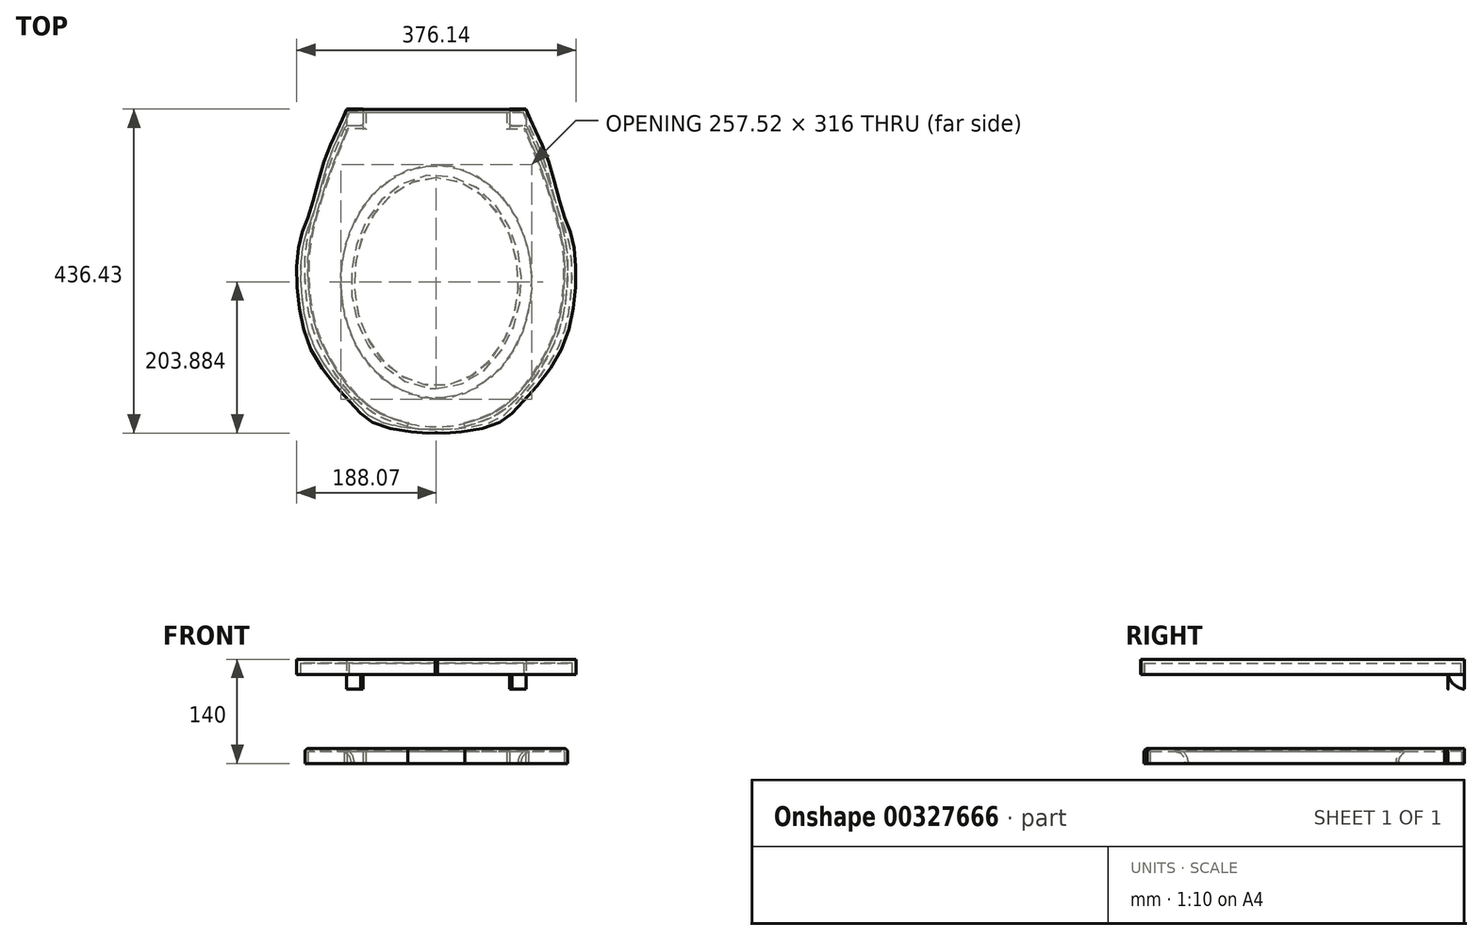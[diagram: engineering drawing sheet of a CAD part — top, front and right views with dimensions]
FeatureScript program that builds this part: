
annotation { "Feature Type Name" : "Feature", "Feature Type Description" : "" }
export const myFeature = defineFeature(function(context is Context, id is Id, definition is map)
    precondition{}
    {
        {
            var Q0;
            Q0=qCreatedBy(makeId("Top.planeOp"),FACE);
            var sketch = newSketch(context, id + "F0", { "sketchPlane" : qUnion([Q0])});
            skEllipse(sketch, "E0", {"center": v(236.1, 282.98) * mm, "majorRadius": 140 * mm, "minorRadius": 110.76 * mm, "majorAxis": v(0, 1)});
            skLineSegment(sketch, "E1", {"start": v(115.12, 515.5) * mm, "end": v(236.1, 515.5) * mm});
            skFitSpline(sketch, "E2", {"points": [v(115.12, 515.5) * mm, v(87.79, 448.56) * mm, v(66.11, 379.92) * mm, v(54.24, 335.02) * mm, v(53.21, 266.89) * mm, v(77.73, 184.39) * mm, v(125, 119.02) * mm, v(164.89, 92.63) * mm, v(226.57, 79.74) * mm, v(235.17, 79.43) * mm, v(240.38, 79.43) * mm], "startDerivative": vector(-235.73, -539.67) * mm, "endDerivative": vector(163.45, -0.98) * mm});
            skLineSegment(sketch, "E3", {"start": v(236.1, 515.5) * mm, "end": v(236.1, 282.98) * mm, "construction": true});
            skFitSpline(sketch, "E4.MirrorCS", {"points": [v(357.1, 515.5) * mm, v(384.43, 448.56) * mm, v(406.1, 379.92) * mm, v(417.98, 335.02) * mm, v(419, 266.89) * mm, v(394.49, 184.39) * mm, v(347.22, 119.02) * mm, v(307.33, 92.63) * mm, v(245.65, 79.74) * mm, v(237.05, 79.43) * mm, v(231.84, 79.43) * mm], "startDerivative": vector(235.73, -539.67) * mm, "endDerivative": vector(-163.45, -0.98) * mm});
            skLineSegment(sketch, "E5.MirrorCS", {"start": v(357.1, 515.5) * mm, "end": v(236.1, 515.5) * mm});
            skLineSegment(sketch, "E6", {"start": v(137.44, 515.5) * mm, "end": v(137.44, 493.2) * mm});
            skLineSegment(sketch, "E7", {"start": v(137.44, 493.2) * mm, "end": v(117.65, 493.2) * mm});
            skLineSegment(sketch, "E8", {"start": v(236.1, 282.98) * mm, "end": v(236.1, 61.07) * mm, "construction": true});
            skArc(sketch, "E9", {"start": v(117.65, 493.2) * mm, "mid": v(114.06, 491.98) * mm, "end": v(111.95, 488.82) * mm});
            skLineSegment(sketch, "E10", {"start": v(236.1, 83.72) * mm, "end": v(197.51, 88.12) * mm, "construction": true});
            skArc(sketch, "E11", {"start": v(197.51, 88.12) * mm, "mid": v(216.69, 84.82) * mm, "end": v(236.1, 83.72) * mm});
            skFitSpline(sketch, "E12", {"points": [v(197.51, 88.12) * mm, v(160.98, 100.68) * mm, v(121.9, 130.72) * mm, v(84.87, 184.45) * mm, v(64.85, 239.02) * mm, v(59.04, 301.02) * mm, v(63.56, 345.58) * mm, v(87.45, 426.95) * mm, v(111.95, 488.82) * mm], "startDerivative": vector(-360.52, 97.38) * mm, "endDerivative": vector(181.28, 430.4) * mm});
            skLineSegment(sketch, "E13.MirrorCS", {"start": v(334.78, 493.2) * mm, "end": v(354.57, 493.2) * mm});
            skLineSegment(sketch, "E14.MirrorCS", {"start": v(334.78, 515.5) * mm, "end": v(334.78, 493.2) * mm});
            skArc(sketch, "E15.MirrorCS", {"start": v(354.57, 493.2) * mm, "mid": v(358.16, 491.98) * mm, "end": v(360.27, 488.82) * mm});
            skFitSpline(sketch, "E16.MirrorCS", {"points": [v(274.7, 88.12) * mm, v(311.24, 100.68) * mm, v(350.31, 130.72) * mm, v(387.35, 184.45) * mm, v(407.37, 239.02) * mm, v(413.18, 301.02) * mm, v(408.66, 345.58) * mm, v(384.77, 426.95) * mm, v(360.27, 488.82) * mm], "startDerivative": vector(360.52, 97.38) * mm, "endDerivative": vector(-181.28, 430.4) * mm});
            skArc(sketch, "E17.MirrorCS", {"start": v(274.7, 88.12) * mm, "mid": v(255.53, 84.82) * mm, "end": v(236.1, 83.72) * mm});
            skLineSegment(sketch, "E18.MirrorCS", {"start": v(236.1, 83.72) * mm, "end": v(274.7, 88.12) * mm, "construction": true});
            skSolve(sketch);
        }
        {
            var Q0;
            Q0=makeQuery(id+"F0.imprint","IMPRINT",FACE,{"disambiguationData":[TD([[makeQuery(id+"F0.imprint","IMPRINT",EDGE,{"derivedFrom":sQuery(id+"F0.wireOp",EDGE,"E0")}),-1.0]])]});
            extrude(context, id + "F1", {"entities" : qUnion([Q0]), "depth" : 20 * mm});
        }
        {
            var Q0;
            Q0=makeQuery(id+"F1.opExtrude","CAP_EDGE",EDGE,{"disambiguationData":[OSD([sQuery(id+"F0.wireOp",EDGE,"E0")])],"isStart":false});
            fillet(context, id + "F2", {"entities" : qUnion([Q0]), "radius" : 18 * mm, "tangentPropagation" : true, "allowEdgeOverflow" : false});
        }
        {
            var Q0;
            Q0=makeQuery(id+"F1.opExtrude","CAP_EDGE",EDGE,{"disambiguationData":[OSD([sQuery(id+"F0.wireOp",EDGE,"E12")])],"isStart":false});
            var Q1;
            Q1=makeQuery(id+"F1.opExtrude","CAP_EDGE",EDGE,{"disambiguationData":[OSD([sQuery(id+"F0.wireOp",EDGE,"E11"),sQuery(id+"F0.wireOp",EDGE,"E17.MirrorCS")])],"isStart":false});
            var Q2;
            Q2=makeQuery(id+"F1.opExtrude","CAP_EDGE",EDGE,{"disambiguationData":[OSD([sQuery(id+"F0.wireOp",EDGE,"E16.MirrorCS")])],"isStart":false});
            var Q3;
            Q3=makeQuery(id+"F1.opExtrude","CAP_EDGE",EDGE,{"disambiguationData":[OSD([sQuery(id+"F0.wireOp",EDGE,"E15.MirrorCS")])],"isStart":false});
            var Q4;
            Q4=makeQuery(id+"F1.opExtrude","CAP_EDGE",EDGE,{"disambiguationData":[OSD([sQuery(id+"F0.wireOp",EDGE,"E13.MirrorCS")])],"isStart":false});
            var Q5;
            Q5=makeQuery(id+"F1.opExtrude","CAP_EDGE",EDGE,{"disambiguationData":[OSD([sQuery(id+"F0.wireOp",EDGE,"E9")])],"isStart":false});
            var Q6;
            Q6=makeQuery(id+"F1.opExtrude","CAP_EDGE",EDGE,{"disambiguationData":[OSD([sQuery(id+"F0.wireOp",EDGE,"E7")])],"isStart":false});
            fillet(context, id + "F3", {"entities" : qUnion([Q0, Q1, Q2, Q3, Q4, Q5, Q6]), "radius" : 5 * mm, "tangentPropagation" : true, "allowEdgeOverflow" : false});
        }
        {
            var Q0;
            Q0=makeQuery(id+"F1.opExtrude","CAP_FACE",FACE,{"disambiguationData":[OSD([sQuery(id+"F0.wireOp",EDGE,"E0"),sQuery(id+"F0.wireOp",EDGE,"E1"),sQuery(id+"F0.wireOp",EDGE,"E5.MirrorCS"),sQuery(id+"F0.wireOp",EDGE,"E6"),sQuery(id+"F0.wireOp",EDGE,"E7"),sQuery(id+"F0.wireOp",EDGE,"98a317c4-5fe9-485b-bc22-271dbf30fffc"),sQuery(id+"F0.wireOp",EDGE,"01ff45cd-890d-4195-a086-3f56b90537150.MirrorCS"),sQuery(id+"F0.wireOp",EDGE,"01ff45cd-890d-4195-a086-3f56b90537151.MirrorCS"),sQuery(id+"F0.wireOp",EDGE,"01ff45cd-890d-4195-a086-3f56b90537152.MirrorCS")])],"isStart":true});
            shell(context, id + "F4", {"entities" : qUnion([Q0]), "thickness" : 4 * mm});
        }
        {
            var Q0;
            Q0=makeQuery(id+"F1.opExtrude","CAP_FACE",FACE,{"disambiguationData":[OSD([sQuery(id+"F0.wireOp",EDGE,"E0"),sQuery(id+"F0.wireOp",EDGE,"E1"),sQuery(id+"F0.wireOp",EDGE,"E5.MirrorCS"),sQuery(id+"F0.wireOp",EDGE,"E6"),sQuery(id+"F0.wireOp",EDGE,"E7"),sQuery(id+"F0.wireOp",EDGE,"E9"),sQuery(id+"F0.wireOp",EDGE,"E11"),sQuery(id+"F0.wireOp",EDGE,"E12"),sQuery(id+"F0.wireOp",EDGE,"E13.MirrorCS"),sQuery(id+"F0.wireOp",EDGE,"E14.MirrorCS"),sQuery(id+"F0.wireOp",EDGE,"E15.MirrorCS"),sQuery(id+"F0.wireOp",EDGE,"E16.MirrorCS"),sQuery(id+"F0.wireOp",EDGE,"E17.MirrorCS")])],"isStart":false});
            cPlane(context, id + "F5", {"entities" : qUnion([Q0]), "cplaneType" : CPlaneType.OFFSET, "offset" : 100 * mm, "width" : 150 * mm, "height" : 150 * mm});
        }
        {
            var Q0;
            Q0=qCreatedBy(id+"F5.planeOp",FACE);
            var sketch = newSketch(context, id + "F6", { "sketchPlane" : qUnion([Q0])});
            skLineSegment(sketch, "E19.0.0", {"start": v(357.1, 515.5) * mm, "end": v(334.78, 515.5) * mm});
            skLineSegment(sketch, "E19.0.11", {"start": v(137.44, 515.5) * mm, "end": v(115.12, 515.5) * mm});
            skFitSpline(sketch, "E19.0.12", {"points": [v(115.12, 515.5) * mm, v(105.63, 493.78) * mm, v(86.66, 450.36) * mm, v(66.5, 379.75) * mm, v(51.66, 335.52) * mm, v(49.53, 264.45) * mm, v(71.71, 183.3) * mm, v(123.62, 116.85) * mm, v(159.22, 89.72) * mm, v(225.54, 79.1) * mm, v(234.58, 79.47) * mm, v(238.62, 79.44) * mm, v(240.38, 79.43) * mm]});
            skFitSpline(sketch, "E19.0.13", {"points": [v(231.84, 79.43) * mm, v(233.6, 79.44) * mm, v(237.64, 79.47) * mm, v(246.68, 79.1) * mm, v(313, 89.72) * mm, v(348.6, 116.85) * mm, v(400.5, 183.3) * mm, v(422.7, 264.45) * mm, v(420.56, 335.52) * mm, v(405.71, 379.75) * mm, v(385.56, 450.36) * mm, v(366.6, 493.78) * mm, v(357.1, 515.5) * mm]});
            skLineSegment(sketch, "E20.0", {"start": v(334.78, 515.5) * mm, "end": v(137.44, 515.5) * mm});
            skLineSegment(sketch, "E21.0", {"start": v(357.1, 515.5) * mm, "end": v(236.1, 515.5) * mm});
            skLineSegment(sketch, "E22.0", {"start": v(115.12, 515.5) * mm, "end": v(236.1, 515.5) * mm});
            skPoint(sketch, "E19.0.10.start.orphan", {"position": v(137.44, 493.2) * mm});
            skPoint(sketch, "E23.orphan", {"position": v(137.44, 488.2) * mm});
            skPoint(sketch, "E19.0.8.end.orphan", {"position": v(117.65, 493.2) * mm});
            skPoint(sketch, "E19.0.7.end.orphan", {"position": v(111.95, 488.82) * mm});
            skPoint(sketch, "E19.0.1.end.orphan", {"position": v(334.78, 493.2) * mm});
            skPoint(sketch, "E19.0.6.end.orphan", {"position": v(197.51, 88.12) * mm});
            skPoint(sketch, "E24.0.4.end.orphan", {"position": v(273.5, 92.97) * mm});
            skPoint(sketch, "E24.0.4.start.orphan", {"position": v(198.72, 92.97) * mm});
            skPoint(sketch, "E19.0.5.end.orphan", {"position": v(236.1, 83.72) * mm});
            skPoint(sketch, "E19.0.5.start.orphan", {"position": v(274.7, 88.12) * mm});
            skPoint(sketch, "E24.0.2.end.orphan", {"position": v(116.75, 487.34) * mm});
            skPoint(sketch, "E24.0.2.start.orphan", {"position": v(117.65, 488.2) * mm});
            skPoint(sketch, "E19.0.3.end.orphan", {"position": v(360.27, 488.82) * mm});
            skPoint(sketch, "E19.0.3.start.orphan", {"position": v(354.57, 493.2) * mm});
            skPoint(sketch, "E24.0.6.end.orphan", {"position": v(354.57, 488.2) * mm});
            skPoint(sketch, "E24.0.6.start.orphan", {"position": v(355.47, 487.34) * mm});
            skPoint(sketch, "E24.0.8.start.orphan", {"position": v(334.78, 488.2) * mm});
            skSolve(sketch);
        }
        {
            var Q0;
            Q0 = qSketchRegion(id + "F6", true);
            extrude(context, id + "F7", {"entities" : qUnion([Q0]), "depth" : 20 * mm});
        }
        {
            var Q0;
            Q0=makeQuery(id+"F7.opExtrude","CAP_FACE",FACE,{"disambiguationData":[OSD([sQuery(id+"F6.wireOp",EDGE,"E19.0.12"),sQuery(id+"F6.wireOp",EDGE,"E19.0.13"),sQuery(id+"F6.wireOp",EDGE,"E21.0"),sQuery(id+"F6.wireOp",EDGE,"E22.0")])],"isStart":true});
            shell(context, id + "F8", {"entities" : qUnion([Q0]), "thickness" : 5 * mm});
        }
        {
            var Q0;
            Q0=qCreatedBy(id+"F5.planeOp",FACE);
            var sketch = newSketch(context, id + "F9", { "sketchPlane" : qUnion([Q0])});
            skLineSegment(sketch, "E25", {"start": v(334.8, 515.53) * mm, "end": v(334.8, 496.05) * mm});
            skLineSegment(sketch, "E26", {"start": v(334.8, 515.53) * mm, "end": v(357.05, 515.53) * mm});
            skLineSegment(sketch, "E27", {"start": v(357.05, 515.53) * mm, "end": v(357.05, 493.36) * mm});
            skLineSegment(sketch, "E28", {"start": v(357.05, 493.36) * mm, "end": v(337.94, 493.36) * mm});
            skArc(sketch, "E29", {"start": v(334.8, 496.05) * mm, "mid": v(335.75, 493.98) * mm, "end": v(337.94, 493.36) * mm});
            skLineSegment(sketch, "E30.MirrorCS", {"start": v(137.42, 515.53) * mm, "end": v(137.42, 496.05) * mm});
            skLineSegment(sketch, "E31.MirrorCS", {"start": v(137.42, 515.53) * mm, "end": v(115.17, 515.53) * mm});
            skLineSegment(sketch, "E32.MirrorCS", {"start": v(115.17, 515.53) * mm, "end": v(115.17, 493.36) * mm});
            skLineSegment(sketch, "E33.MirrorCS", {"start": v(115.17, 493.36) * mm, "end": v(134.28, 493.36) * mm});
            skArc(sketch, "E34.MirrorCS", {"start": v(137.42, 496.05) * mm, "mid": v(136.47, 493.98) * mm, "end": v(134.28, 493.36) * mm});
            skSolve(sketch);
        }
        {
            var Q0;
            Q0 = qSketchRegion(id + "F9", true);
            extrude(context, id + "F10", {"entities" : qUnion([Q0]), "operationType" : NewBodyOperationType.ADD, "oppositeDirection" : true, "depth" : 20 * mm});
        }
        {
            var Q0;
            Q0=qCreatedBy(makeId("Right.planeOp"),FACE);
            var sketch = newSketch(context, id + "F11", { "sketchPlane" : qUnion([Q0])});
            skArc(sketch, "E35", {"start": v(493.36, 120) * mm, "mid": v(501.14, 106.33) * mm, "end": v(515.54, 100) * mm});
            skLineSegment(sketch, "E36", {"start": v(493.36, 120) * mm, "end": v(493.36, 99.97) * mm});
            skLineSegment(sketch, "E37", {"start": v(493.36, 99.97) * mm, "end": v(515.54, 100) * mm});
            skSolve(sketch);
        }
        {
            var Q0;
            Q0=makeQuery(id+"F11.imprint","IMPRINT",FACE,{"disambiguationData":[TD([[makeQuery(id+"F11.imprint","IMPRINT",EDGE,{"derivedFrom":sQuery(id+"F11.wireOp",EDGE,"E35")}),-1.0]])]});
            extrude(context, id + "F12", {"entities" : qUnion([Q0]), "operationType" : NewBodyOperationType.REMOVE, "endBound" : BoundingType.THROUGH_ALL, "depth" : 25 * mm});
        }
    });
